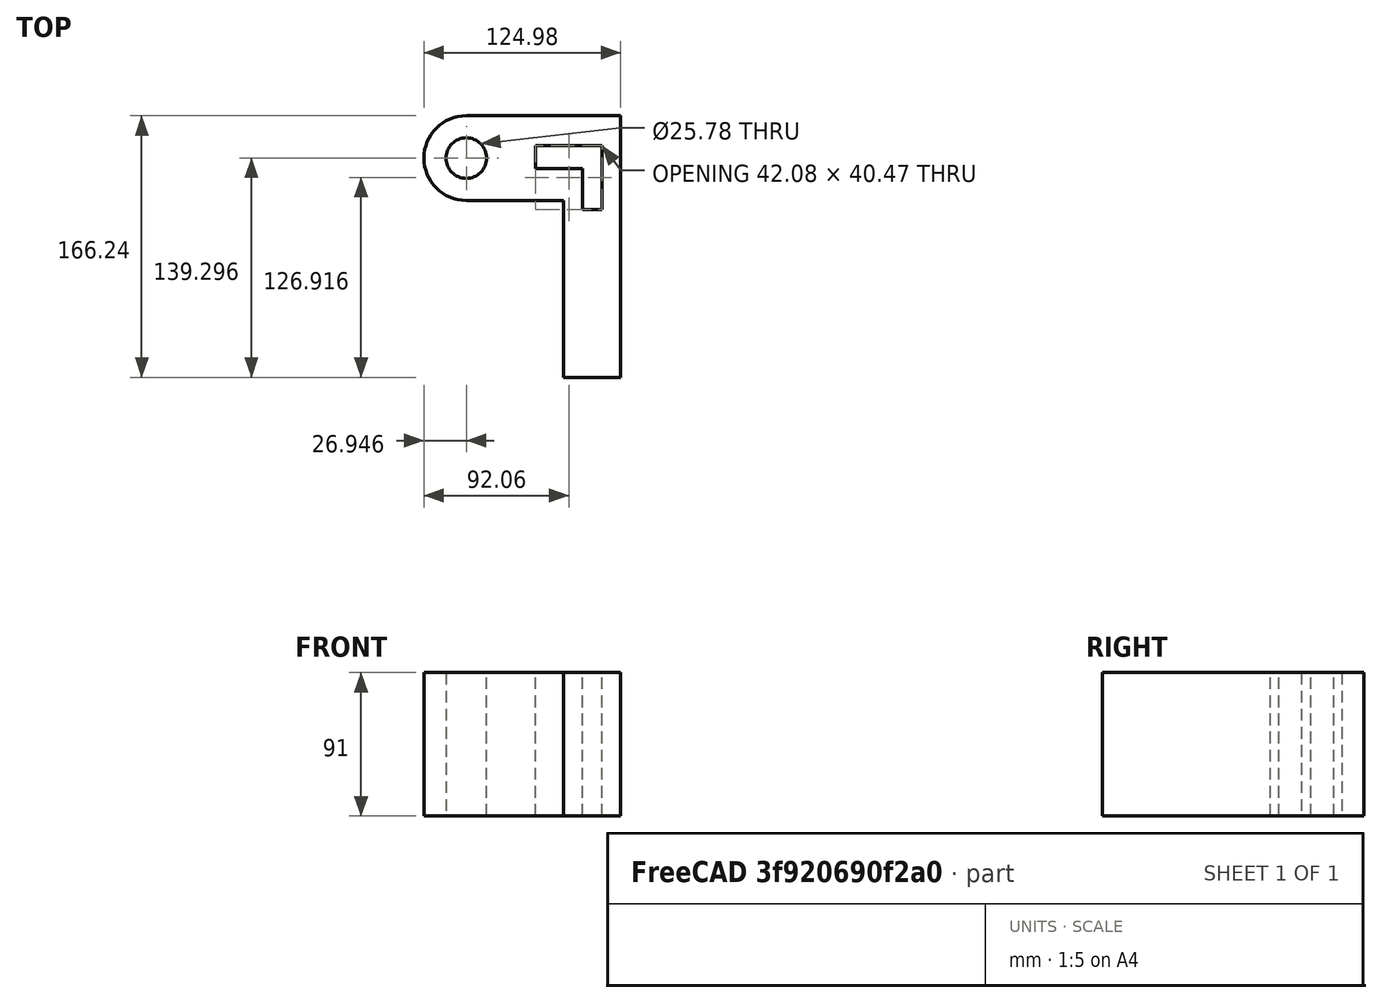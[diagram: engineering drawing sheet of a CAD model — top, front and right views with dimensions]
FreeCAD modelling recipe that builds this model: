
FCSTD DOCUMENT
Label: Fem
License: CC-BY 3.0
LicenseURL: http://creativecommons.org/licenses/by/3.0/
objects: Sketcher::SketchObject×1, PartDesign::Pad×1, Fem::FemMeshShapeObject×1, Fem::ConstraintFixed×1, Fem::ConstraintForce×1
note: 3 computed .brp shape members not serialized (recipe doc carries the construction recipe); baked Part::Feature solids carry a one-line shape summary decoded from their .brp

FEATURE [Sketcher::SketchObject] Sketch
  sketch-geometry (13):
    g0: ArcOfCircle CenterX=-29.9237 CenterY=19.9863 CenterZ=0 NormalX=0 NormalY=0 NormalZ=1 Radius=26.9466 StartAngle=1.5708 EndAngle=4.71239
    g1: LineSegment StartX=-29.9237 StartY=46.933 StartZ=0 EndX=68.1073 EndY=46.933 EndZ=0
    g2: LineSegment StartX=68.1073 StartY=46.933 StartZ=0 EndX=68.1073 EndY=-119.309 EndZ=0
    g3: LineSegment StartX=68.1073 StartY=-119.309 StartZ=0 EndX=31.7141 EndY=-119.309 EndZ=0
    g4: LineSegment StartX=31.7141 StartY=-119.309 StartZ=0 EndX=31.7141 EndY=-6.96029 EndZ=0
    g5: LineSegment StartX=31.7141 StartY=-6.96029 StartZ=0 EndX=-29.9236 EndY=-6.96029 EndZ=0
    g6: Circle CenterX=-29.9237 CenterY=19.9863 CenterZ=0 NormalX=0 NormalY=0 NormalZ=1 Radius=12.8881
    g7: LineSegment StartX=14.1478 StartY=27.839 StartZ=0 EndX=56.2317 EndY=27.839 EndZ=0
    g8: LineSegment StartX=56.2317 StartY=27.839 StartZ=0 EndX=56.2317 EndY=-12.6263 EndZ=0
    g9: LineSegment StartX=56.2317 StartY=-12.6263 StartZ=0 EndX=43.9303 EndY=-12.6263 EndZ=0
    g10: LineSegment StartX=43.9303 StartY=-12.6263 StartZ=0 EndX=43.9303 EndY=13.2715 EndZ=0
    g11: LineSegment StartX=43.9303 StartY=13.2715 StartZ=0 EndX=14.1478 EndY=13.2715 EndZ=0
    g12: LineSegment StartX=14.1478 StartY=13.2715 StartZ=0 EndX=14.1478 EndY=27.839 EndZ=0
  constraints (25):
    c: Tangent(g0,g1)
    c: Coincident(g1,g2)
    c: Vertical(g2)
    c: Coincident(g2,g3)
    c: Horizontal(g3)
    c: Coincident(g3,g4)
    c: Vertical(g4)
    c: Coincident(g4,g5)
    c: Coincident(g5,g0)
    c: Horizontal(g5)
    c: Horizontal(g1)
    c: Tangent(g0,g5)
    c: Coincident(g6,g0)
    c: Horizontal(g7)
    c: Coincident(g7,g8)
    c: Vertical(g8)
    c: Coincident(g8,g9)
    c: Horizontal(g9)
    c: Coincident(g9,g10)
    c: Vertical(g10)
    c: Coincident(g10,g11)
    c: Horizontal(g11)
    c: Coincident(g11,g12)
    c: Coincident(g12,g7)
    c: Vertical(g12)
FEATURE [PartDesign::Pad] Pad
  Length = 91
  Length2 = 100
  Sketch = -> Sketch
  Type = 0
FEATURE [Fem::FemMeshShapeObject] FemShape
  Shape = -> Pad
FEATURE [Fem::ConstraintFixed] FemConstraintFixed
  NormalDirection = (0,-1,0)
  References = -> [Pad]
FEATURE [Fem::ConstraintForce] FemConstraintForce
  DirectionVector = (-1,-2.3988e-07,0)
  Force = 0
  NormalDirection = (-1,-2.3988e-07,0)
  References = -> [Pad]
